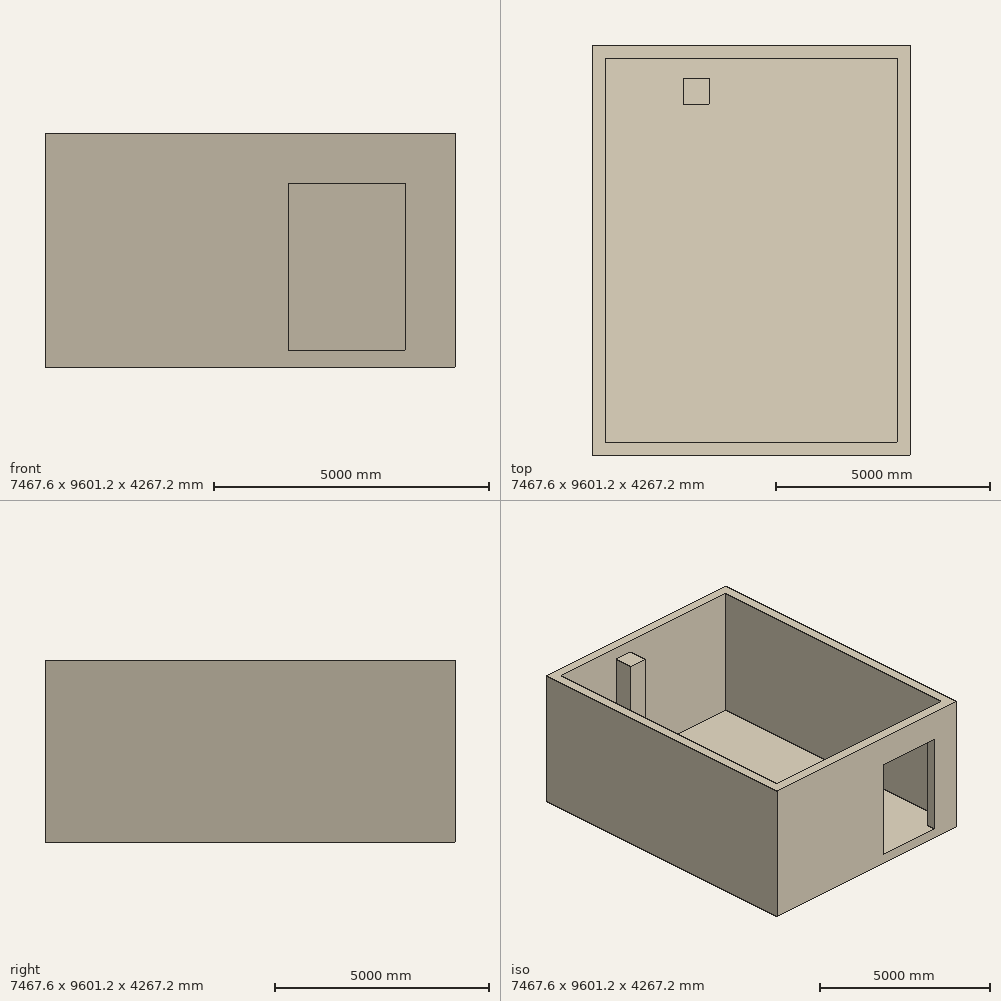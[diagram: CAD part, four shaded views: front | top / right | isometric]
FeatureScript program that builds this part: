
annotation { "Feature Type Name" : "Feature", "Feature Type Description" : "" }
export const myFeature = defineFeature(function(context is Context, id is Id, definition is map)
    precondition{}
    {
        {
            var Q0;
            Q0=qCreatedBy(makeId("Top.planeOp"),FACE);
            var sketch = newSketch(context, id + "F0", { "sketchPlane" : qUnion([Q0])});
            skLineSegment(sketch, "E0.bottom", {"start": v(3733.8, -4800.6) * mm, "end": v(-3733.8, -4800.6) * mm});
            skLineSegment(sketch, "E0.top", {"start": v(3733.8, 4800.6) * mm, "end": v(-3733.8, 4800.6) * mm});
            skLineSegment(sketch, "E0.left", {"start": v(3733.8, -4800.6) * mm, "end": v(3733.8, 4800.6) * mm});
            skLineSegment(sketch, "E0.right", {"start": v(-3733.8, -4800.6) * mm, "end": v(-3733.8, 4800.6) * mm});
            skPoint(sketch, "E0.middle", {"position": v(0, 0) * mm});
            skSolve(sketch);
        }
        {
            var Q0;
            Q0 = qSketchRegion(id + "F0", true);
            extrude(context, id + "F1", {"entities" : qUnion([Q0]), "depth" : 4267.2 * mm, "offsetDistance" : 25.4 * mm});
        }
        {
            var Q0;
            Q0=makeQuery(id+"F1.opExtrude","CAP_FACE",FACE,{"disambiguationData":[OSD([sQuery(id+"F0.wireOp",EDGE,"E0.bottom"),sQuery(id+"F0.wireOp",EDGE,"E0.top"),sQuery(id+"F0.wireOp",EDGE,"E0.left"),sQuery(id+"F0.wireOp",EDGE,"E0.right")])],"isStart":false});
            var sketch = newSketch(context, id + "F2", { "sketchPlane" : qUnion([Q0])});
            skLineSegment(sketch, "E1.bottom", {"start": v(3429, -4495.8) * mm, "end": v(-3429, -4495.8) * mm});
            skLineSegment(sketch, "E1.top", {"start": v(3429, 4495.8) * mm, "end": v(-3429, 4495.8) * mm});
            skLineSegment(sketch, "E1.left", {"start": v(3429, -4495.8) * mm, "end": v(3429, 4495.8) * mm});
            skLineSegment(sketch, "E1.right", {"start": v(-3429, -4495.8) * mm, "end": v(-3429, 4495.8) * mm});
            skPoint(sketch, "E1.middle", {"position": v(0, 0) * mm});
            skSolve(sketch);
        }
        {
            var Q0;
            Q0 = qSketchRegion(id + "F2", true);
            extrude(context, id + "F3", {"entities" : qUnion([Q0]), "operationType" : NewBodyOperationType.REMOVE, "oppositeDirection" : true, "depth" : 3962.4 * mm, "offsetDistance" : 25.4 * mm});
        }
        {
            var Q0;
            Q0=makeQuery(id+"F3.boolean.opBoolean","COPY",FACE,{"derivedFrom":makeQuery(id+"F3.opExtrude","CAP_FACE",FACE,{"disambiguationData":[OSD([sQuery(id+"F2.wireOp",EDGE,"E1.bottom"),sQuery(id+"F2.wireOp",EDGE,"E1.top"),sQuery(id+"F2.wireOp",EDGE,"E1.left"),sQuery(id+"F2.wireOp",EDGE,"E1.right")])],"isStart":false})});
            var sketch = newSketch(context, id + "F4", { "sketchPlane" : qUnion([Q0])});
            skLineSegment(sketch, "E2.bottom", {"start": v(-1600.2, 4038.6) * mm, "end": v(-990.6, 4038.6) * mm});
            skLineSegment(sketch, "E2.top", {"start": v(-1600.2, 3429) * mm, "end": v(-990.6, 3429) * mm});
            skLineSegment(sketch, "E2.left", {"start": v(-1600.2, 4038.6) * mm, "end": v(-1600.2, 3429) * mm});
            skLineSegment(sketch, "E2.right", {"start": v(-990.6, 4038.6) * mm, "end": v(-990.6, 3429) * mm});
            skSolve(sketch);
        }
        {
            var Q0;
            Q0 = qSketchRegion(id + "F4", true);
            extrude(context, id + "F5", {"entities" : qUnion([Q0]), "operationType" : NewBodyOperationType.ADD, "depth" : 3962.4 * mm, "offsetDistance" : 25.4 * mm});
        }
        {
            var Q0;
            Q0=makeQuery(id+"F1.opExtrude","SWEPT_FACE",FACE,{"disambiguationData":[OSD([sQuery(id+"F0.wireOp",EDGE,"E0.bottom")])]});
            var sketch = newSketch(context, id + "F6", { "sketchPlane" : qUnion([Q0])});
            skLineSegment(sketch, "E3.bottom", {"start": v(685.8, 3352.8) * mm, "end": v(2819.4, 3352.8) * mm});
            skLineSegment(sketch, "E3.top", {"start": v(685.8, 304.8) * mm, "end": v(2819.4, 304.8) * mm});
            skLineSegment(sketch, "E3.left", {"start": v(685.8, 3352.8) * mm, "end": v(685.8, 304.8) * mm});
            skLineSegment(sketch, "E3.right", {"start": v(2819.4, 3352.8) * mm, "end": v(2819.4, 304.8) * mm});
            skSolve(sketch);
        }
        {
            var Q0;
            Q0 = qSketchRegion(id + "F6", true);
            extrude(context, id + "F7", {"entities" : qUnion([Q0]), "operationType" : NewBodyOperationType.REMOVE, "endBound" : BoundingType.UP_TO_NEXT, "oppositeDirection" : true, "depth" : 25.4 * mm, "offsetDistance" : 25.4 * mm});
        }
    });
